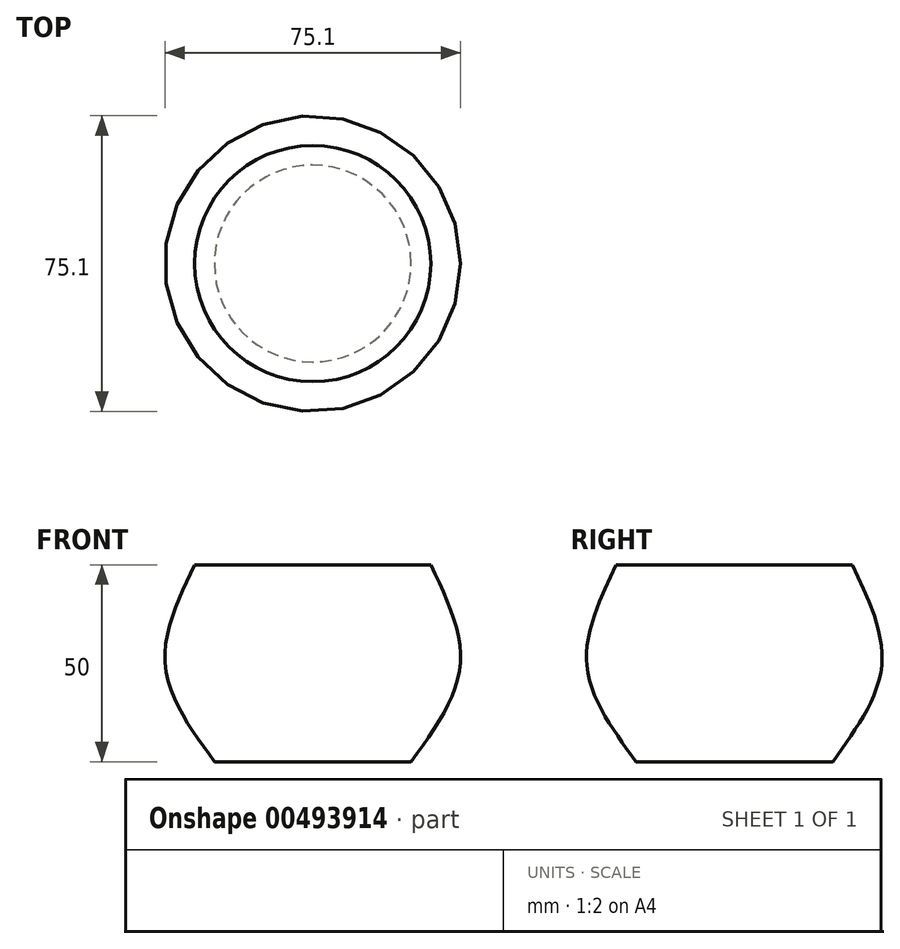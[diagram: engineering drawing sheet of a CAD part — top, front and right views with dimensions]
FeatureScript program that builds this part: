
annotation { "Feature Type Name" : "Feature", "Feature Type Description" : "" }
export const myFeature = defineFeature(function(context is Context, id is Id, definition is map)
    precondition{}
    {
        {
            var Q0;
            Q0=qCreatedBy(makeId("Top.planeOp"),FACE);
            cPlane(context, id + "F0", {"entities" : qUnion([Q0]), "cplaneType" : CPlaneType.OFFSET, "offset" : 25 * mm, "width" : 150 * mm, "height" : 150 * mm});
        }
        {
            var Q0;
            Q0=qCreatedBy(id+"F0.planeOp",FACE);
            cPlane(context, id + "F1", {"entities" : qUnion([Q0]), "cplaneType" : CPlaneType.OFFSET, "offset" : 25 * mm, "width" : 150 * mm, "height" : 150 * mm});
        }
        {
            var Q0;
            Q0=qCreatedBy(makeId("Top.planeOp"),FACE);
            var sketch = newSketch(context, id + "F2", { "sketchPlane" : qUnion([Q0])});
            skCircle(sketch, "E0", {"center": v(0, 0) * mm, "radius": 25 * mm});
            skSolve(sketch);
        }
        {
            var Q0;
            Q0=qCreatedBy(id+"F0.planeOp",FACE);
            var sketch = newSketch(context, id + "F3", { "sketchPlane" : qUnion([Q0])});
            skCircle(sketch, "E1", {"center": v(0, 0) * mm, "radius": 37.5 * mm});
            skSolve(sketch);
        }
        {
            var Q0;
            Q0=qCreatedBy(id+"F1.planeOp",FACE);
            var sketch = newSketch(context, id + "F4", { "sketchPlane" : qUnion([Q0])});
            skCircle(sketch, "E2", {"center": v(0, 0) * mm, "radius": 30 * mm});
            skSolve(sketch);
        }
        {
            var Q0;
            Q0=makeQuery(id+"F2.imprint","IMPRINT",FACE,{"disambiguationData":[TD([[makeQuery(id+"F2.imprint","IMPRINT",EDGE,{"derivedFrom":sQuery(id+"F2.wireOp",EDGE,"E0")}),1.0]])]});
            var Q1;
            Q1=makeQuery(id+"F3.imprint","IMPRINT",FACE,{"disambiguationData":[TD([[makeQuery(id+"F3.imprint","IMPRINT",EDGE,{"derivedFrom":sQuery(id+"F3.wireOp",EDGE,"E1")}),1.0]])]});
            var Q2;
            Q2=makeQuery(id+"F4.imprint","IMPRINT",FACE,{"disambiguationData":[TD([[makeQuery(id+"F4.imprint","IMPRINT",EDGE,{"derivedFrom":sQuery(id+"F4.wireOp",EDGE,"E2")}),1.0]])]});
            loft(context, id + "F5", {"sheetProfilesArray" : [{ "sheetProfileEntities" : qUnion([Q0]) }, { "sheetProfileEntities" : qUnion([Q1]) }, { "sheetProfileEntities" : qUnion([Q2]) }]});
        }
    });
